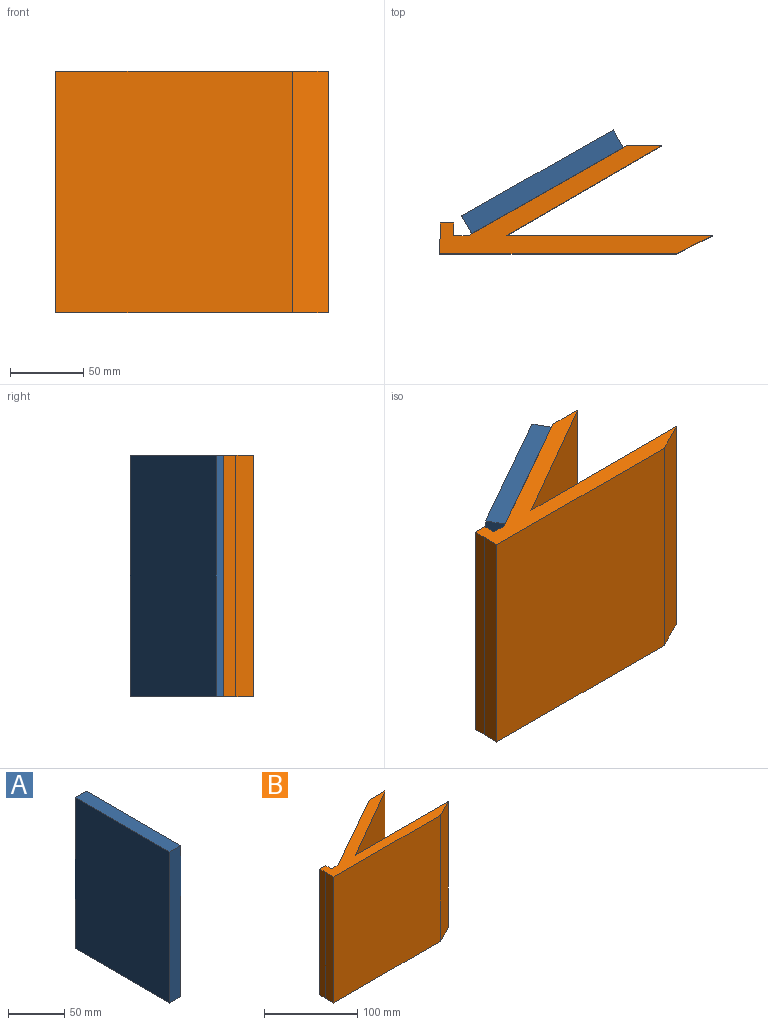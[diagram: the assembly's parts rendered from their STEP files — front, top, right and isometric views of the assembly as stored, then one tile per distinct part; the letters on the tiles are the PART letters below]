
ASSEMBLY  parts=2 mates=1
PART A: 6 faces, bbox 14x119x164 mm
  f0: plane 164x14mm, normal (0,1,0), area 2296mm2, adj f1,f3,f4,f5
  f1: plane 164x119mm, normal (-1,0,0), area 19516mm2, adj f0,f2,f4,f5
  f2: plane 164x14mm, normal (0,-1,0), area 2296mm2, adj f1,f3,f4,f5
  f3: plane 164x119mm, normal (1,0,0), area 19516mm2, adj f0,f2,f4,f5
  f4: plane 119x14mm, normal (0,0,1), area 1666mm2, adj f0,f1,f2,f3
  f5: plane 119x14mm, normal (0,0,-1), area 1666mm2, adj f0,f1,f2,f3
PART B: 13 faces, bbox 186.1x73.8x165 mm
  f0: plane 165x106.52mm, normal (0.5,-0.87,0), area 20295mm2, adj f1,f10,f11,f12
  f1: plane 165x23.99mm, normal (0,1,0), area 3958.4mm2, adj f0,f2,f11,f12
  f2: plane 165x108.31mm, normal (-0.49,0.87,0), area 20550.5mm2, adj f1,f3,f11,f12
  f3: plane 165x10.14mm, normal (0,1,0), area 1672.7mm2, adj f2,f4,f11,f12
  f4: plane 165x8.68mm, normal (1,0,0), area 1432.9mm2, adj f3,f5,f11,f12
  f5: plane 165x9.2mm, normal (0,1,0), area 1517.6mm2, adj f4,f6,f11,f12
  f6: plane 165x8.68mm, normal (-1,0,0), area 1432.9mm2, adj f5,f7,f11,f12
  f7: plane 165x12.3mm, normal (-1,0.01,0), area 2028.9mm2, adj f6,f8,f11,f12
  f8: plane 165x161.71mm, normal (0,-1,0), area 26681.4mm2, adj f7,f9,f11,f12
  f9: plane 165x24.41mm, normal (0.45,-0.89,0), area 4509.8mm2, adj f8,f10,f11,f12
  f10: plane 165x140.83mm, normal (0,1,0), area 23237mm2, adj f0,f9,f11,f12
  f11: plane 186.12x73.8mm, normal (0,0,1), area 3747.3mm2, adj f0,f1,f2,f3,f4,f5,f6,f7
  f12: plane 186.12x73.8mm, normal (0,0,-1), area 3747.3mm2, adj f0,f1,f2,f3,f4,f5,f6,f7
PLACE A rot(axis=(0,0,-1),60.4deg) t=(82.09,-94.3,-23.17)mm
PLACE B t=(-84.88,-27.74,-23.67)mm
MATE parallel A.f3 <-> B.f2  axis (0.49,-0.87,0) through (-172.92,-43.27,58.83)mm
